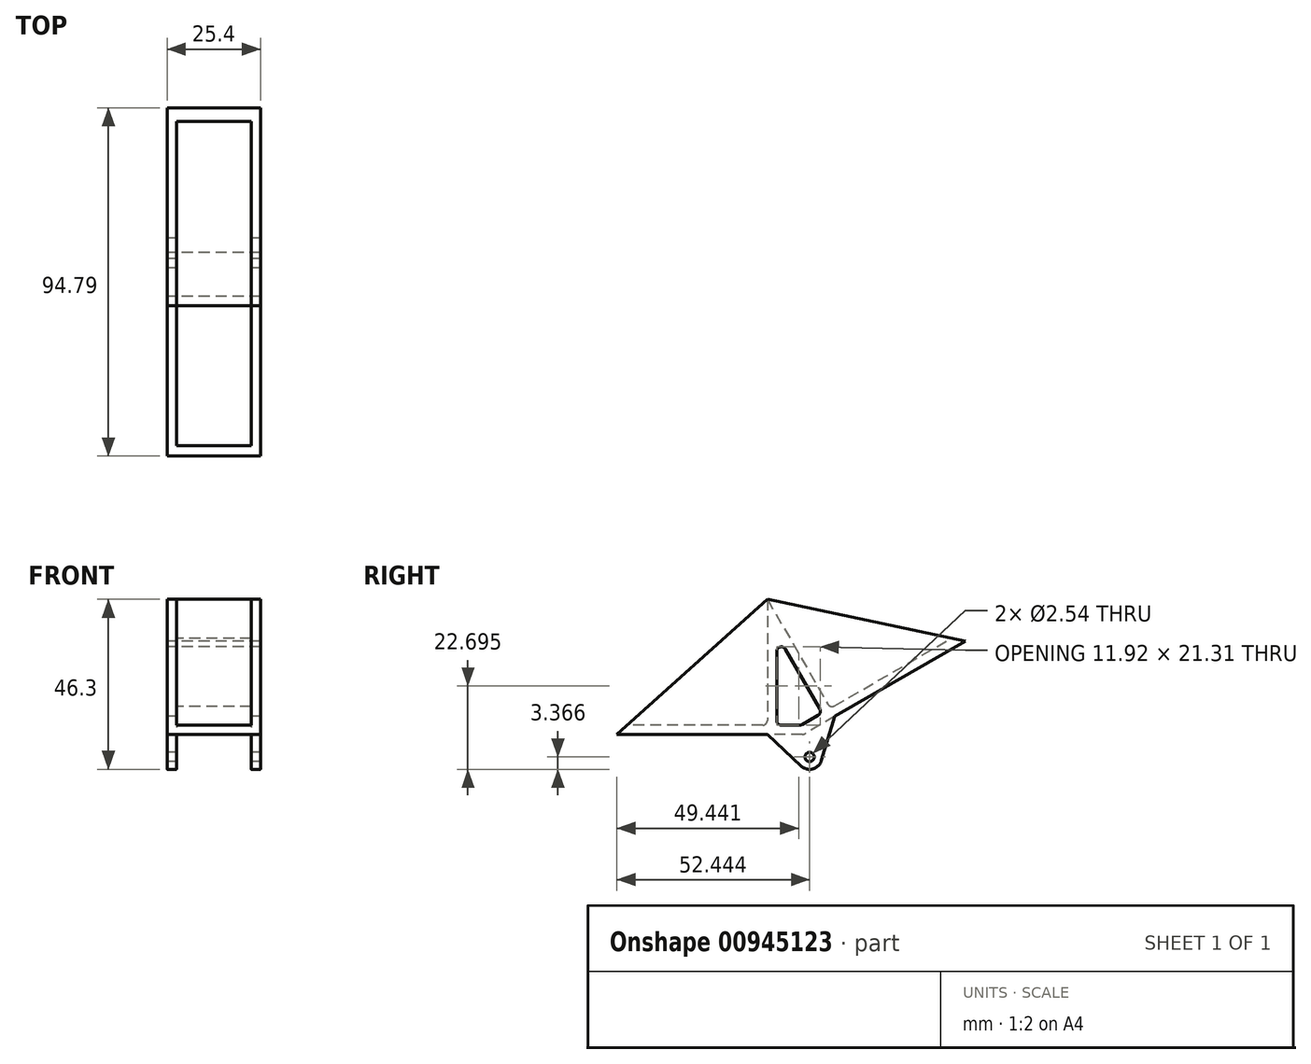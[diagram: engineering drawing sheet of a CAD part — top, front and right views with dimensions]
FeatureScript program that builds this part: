
annotation { "Feature Type Name" : "Feature", "Feature Type Description" : "" }
export const myFeature = defineFeature(function(context is Context, id is Id, definition is map)
    precondition{}
    {
        {
            var Q0;
            Q0=qCreatedBy(makeId("Right.planeOp"),FACE);
            var sketch = newSketch(context, id + "F0", { "sketchPlane" : qUnion([Q0])});
            skLineSegment(sketch, "E0", {"start": v(-9.86, 0) * mm, "end": v(-50.8, 0) * mm});
            skLineSegment(sketch, "E1", {"start": v(8.54, 4.93) * mm, "end": v(44, 25.4) * mm});
            skLineSegment(sketch, "E2", {"start": v(0, 0) * mm, "end": v(-9.86, 36.8) * mm, "construction": true});
            skLineSegment(sketch, "E3", {"start": v(-50.8, 0) * mm, "end": v(-9.86, 36.8) * mm});
            skLineSegment(sketch, "E4", {"start": v(-9.86, 36.8) * mm, "end": v(-8.36, 36.48) * mm});
            skLineSegment(sketch, "E5", {"start": v(-6.05, 2.54) * mm, "end": v(-1.02, 2.54) * mm});
            skLineSegment(sketch, "E6", {"start": v(-0.39, 2.71) * mm, "end": v(3.97, 5.23) * mm});
            skLineSegment(sketch, "E7.trimOffspring", {"start": v(-8.36, 36.48) * mm, "end": v(44, 25.4) * mm});
            skLineSegment(sketch, "E8", {"start": v(-9.86, 36.8) * mm, "end": v(-9.86, 3.81) * mm});
            skLineSegment(sketch, "E9", {"start": v(-9.86, 36.8) * mm, "end": v(6.63, 8.23) * mm});
            skLineSegment(sketch, "E10", {"start": v(-7.32, 3.81) * mm, "end": v(-7.32, 22.58) * mm});
            skLineSegment(sketch, "E11", {"start": v(4.44, 6.96) * mm, "end": v(-4.95, 23.22) * mm});
            skLineSegment(sketch, "E12", {"start": v(0, 0) * mm, "end": v(2.51, -9.38) * mm, "construction": true});
            skLineSegment(sketch, "E13", {"start": v(-0.65, -8.6) * mm, "end": v(-9.86, 0) * mm});
            skLineSegment(sketch, "E14", {"start": v(4.86, -7.12) * mm, "end": v(8.54, 4.93) * mm});
            skLineSegment(sketch, "E15", {"start": v(1.64, -6.13) * mm, "end": v(9.67, -3.98) * mm, "construction": true});
            skArc(sketch, "E16", {"start": v(-0.65, -8.6) * mm, "mid": v(2.51, -9.38) * mm, "end": v(4.86, -7.12) * mm});
            skCircle(sketch, "E17", {"center": v(1.64, -6.13) * mm, "radius": 1.27 * mm});
            skPoint(sketch, "E18.orphan", {"position": v(3.29, -12.27) * mm});
            skArc(sketch, "E19.filletArc", {"start": v(-7.32, 3.81) * mm, "mid": v(-6.95, 2.91) * mm, "end": v(-6.05, 2.54) * mm});
            skArc(sketch, "E20.filletArc", {"start": v(3.97, 5.23) * mm, "mid": v(4.56, 6) * mm, "end": v(4.44, 6.96) * mm});
            skPoint(sketch, "E21.visualSharp", {"position": v(-7.32, 27.32) * mm});
            skArc(sketch, "E21.filletArc", {"start": v(-4.95, 23.22) * mm, "mid": v(-6.38, 23.8) * mm, "end": v(-7.32, 22.58) * mm});
            skLineSegment(sketch, "E22", {"start": v(8.37, 7.77) * mm, "end": v(40.28, 26.19) * mm});
            skArc(sketch, "E23.filletArc", {"start": v(6.63, 8.23) * mm, "mid": v(7.4, 7.64) * mm, "end": v(8.37, 7.77) * mm});
            skLineSegment(sketch, "E24", {"start": v(-11.13, 2.54) * mm, "end": v(-47.97, 2.54) * mm});
            skArc(sketch, "E25.filletArc", {"start": v(-11.13, 2.54) * mm, "mid": v(-10.23, 2.91) * mm, "end": v(-9.86, 3.81) * mm});
            skPoint(sketch, "E26.visualSharp", {"position": v(-0.68, 2.54) * mm});
            skArc(sketch, "E26.filletArc", {"start": v(-1.02, 2.54) * mm, "mid": v(-0.7, 2.58) * mm, "end": v(-0.39, 2.71) * mm});
            skSolve(sketch);
        }
        {
            var Q0;
            {var subQ0=sQuery(id+"F0.wireOp",EDGE,"E3");var subQ1=sQuery(id+"F0.wireOp",EDGE,"E0");var subQ2=makeQuery(id+"F0.imprint","INTERSECT",VERTEX,{"derivedFrom":[subQ1,subQ0]});Q0=makeQuery(id+"F0.imprint","IMPRINT",FACE,{"disambiguationData":[TD([[makeQuery(id+"F0.imprint","IMPRINT",EDGE,{"disambiguationData":[TD([[subQ2,1.0]])],"derivedFrom":subQ1}),-1.0]])]});}
            var Q1;
            {var subQ0=sQuery(id+"F0.wireOp",EDGE,"E4");var subQ1=sQuery(id+"F0.wireOp",EDGE,"E1");var subQ2=makeQuery(id+"F0.imprint","INTERSECT",VERTEX,{"derivedFrom":[subQ1,subQ0]});Q1=makeQuery(id+"F0.imprint","IMPRINT",FACE,{"disambiguationData":[TD([[makeQuery(id+"F0.imprint","IMPRINT",EDGE,{"disambiguationData":[TD([[subQ2,1.0]])],"derivedFrom":subQ1}),1.0]])]});}
            var Q2;
            {var subQ0=sQuery(id+"F0.wireOp",EDGE,"E3");var subQ5=sQuery(id+"F0.wireOp",EDGE,"mqJMZl8p-9VAi-v6qv-n27a-5pC9XECVYwVC");var subQ6=makeQuery(id+"F0.imprint","INTERSECT",VERTEX,{"derivedFrom":[subQ0,subQ5]});Q2=makeQuery(id+"F0.imprint","IMPRINT",FACE,{"disambiguationData":[TD([[makeQuery(id+"F0.imprint","IMPRINT",EDGE,{"disambiguationData":[TD([[subQ6,-1.0]])],"derivedFrom":subQ5}),1.0]])]});}
            var Q3;
            {var subQ0=sQuery(id+"F0.wireOp",EDGE,"E4");var subQ5=sQuery(id+"F0.wireOp",EDGE,"HMWGG6RR-jJKV-HD6m-htNB-dgS0oFNWxqNd");var subQ6=makeQuery(id+"F0.imprint","INTERSECT",VERTEX,{"derivedFrom":[subQ0,subQ5]});Q3=makeQuery(id+"F0.imprint","IMPRINT",FACE,{"disambiguationData":[TD([[makeQuery(id+"F0.imprint","IMPRINT",EDGE,{"disambiguationData":[TD([[subQ6,1.0]])],"derivedFrom":subQ5}),1.0]])]});}
            var Q4;
            {var subQ0=sQuery(id+"F0.wireOp",EDGE,"2FNbGdT5-oPHb-nvho-1RKC-4htPkp7pQmcZ");var subQ1=sQuery(id+"F0.wireOp",EDGE,"E2");var subQ2=makeQuery(id+"F0.imprint","INTERSECT",VERTEX,{"derivedFrom":[subQ1,subQ0]});Q4=makeQuery(id+"F0.imprint","IMPRINT",FACE,{"disambiguationData":[TD([[makeQuery(id+"F0.imprint","IMPRINT",EDGE,{"disambiguationData":[TD([[subQ2,-1.0]])],"derivedFrom":subQ1}),1.0]])]});}
            var Q5;
            {var subQ0=sQuery(id+"F0.wireOp",EDGE,"3LhKCgj5-OBTh-ZDzE-TMFg-cuMuyVttlFuA");var subQ1=sQuery(id+"F0.wireOp",EDGE,"HMWGG6RR-jJKV-HD6m-htNB-dgS0oFNWxqNd");var subQ2=makeQuery(id+"F0.imprint","INTERSECT",VERTEX,{"derivedFrom":[subQ1,subQ0]});Q5=makeQuery(id+"F0.imprint","IMPRINT",FACE,{"disambiguationData":[TD([[makeQuery(id+"F0.imprint","IMPRINT",EDGE,{"disambiguationData":[TD([[subQ2,-1.0]])],"derivedFrom":subQ1}),1.0]])]});}
            extrude(context, id + "F1", {"entities" : qUnion([Q0, Q1, Q2, Q3, Q4, Q5]), "depth" : 25.4 * mm, "offsetDistance" : 25.4 * mm});
        }
        {
            var Q0;
            {var subQ0=sQuery(id+"F0.wireOp",EDGE,"E8");Q0=makeQuery(id+"F0.imprint","IMPRINT",FACE,{"disambiguationData":[TD([[makeQuery(id+"F0.imprint","IMPRINT",EDGE,{"derivedFrom":subQ0}),-1.0]])]});}
            var Q1;
            {var subQ2=sQuery(id+"F0.wireOp",EDGE,"E4");Q1=makeQuery(id+"F0.imprint","IMPRINT",FACE,{"disambiguationData":[TD([[makeQuery(id+"F0.imprint","IMPRINT",EDGE,{"derivedFrom":subQ2}),-1.0]])]});}
            extrude(context, id + "F2", {"entities" : qUnion([Q0, Q1]), "operationType" : NewBodyOperationType.ADD, "depth" : 2.54 * mm, "offsetDistance" : 25.4 * mm});
        }
        {
            var Q0;
            Q0=makeQuery(id+"F1.opExtrude","CAP_FACE",FACE,{"disambiguationData":[OSD([sQuery(id+"F0.wireOp",EDGE,"E0"),sQuery(id+"F0.wireOp",EDGE,"E1"),sQuery(id+"F0.wireOp",EDGE,"E3"),sQuery(id+"F0.wireOp",EDGE,"E5"),sQuery(id+"F0.wireOp",EDGE,"E6"),sQuery(id+"F0.wireOp",EDGE,"E7.trimOffspring"),sQuery(id+"F0.wireOp",EDGE,"E8"),sQuery(id+"F0.wireOp",EDGE,"E9"),sQuery(id+"F0.wireOp",EDGE,"E10"),sQuery(id+"F0.wireOp",EDGE,"E11"),sQuery(id+"F0.wireOp",EDGE,"E13"),sQuery(id+"F0.wireOp",EDGE,"E14"),sQuery(id+"F0.wireOp",EDGE,"E16"),sQuery(id+"F0.wireOp",EDGE,"E17"),sQuery(id+"F0.wireOp",EDGE,"E19.filletArc"),sQuery(id+"F0.wireOp",EDGE,"E20.filletArc"),sQuery(id+"F0.wireOp",EDGE,"E21.filletArc"),sQuery(id+"F0.wireOp",EDGE,"E22"),sQuery(id+"F0.wireOp",EDGE,"E23.filletArc"),sQuery(id+"F0.wireOp",EDGE,"E24"),sQuery(id+"F0.wireOp",EDGE,"E25.filletArc"),sQuery(id+"F0.wireOp",EDGE,"E26.filletArc")])],"isStart":false});
            var sketch = newSketch(context, id + "F3", { "sketchPlane" : qUnion([Q0])});
            skLineSegment(sketch, "E27.0.0", {"start": v(-9.86, 36.8) * mm, "end": v(-47.97, 2.54) * mm});
            skLineSegment(sketch, "E27.0.1", {"start": v(-47.97, 2.54) * mm, "end": v(-11.13, 2.54) * mm});
            skArc(sketch, "E27.0.2", {"start": v(-11.13, 2.54) * mm, "mid": v(-10.23, 2.91) * mm, "end": v(-9.86, 3.81) * mm});
            skLineSegment(sketch, "E27.0.3", {"start": v(-9.86, 3.81) * mm, "end": v(-9.86, 36.8) * mm});
            skLineSegment(sketch, "E28.0.0", {"start": v(40.28, 26.19) * mm, "end": v(-9.86, 36.8) * mm});
            skLineSegment(sketch, "E28.0.1", {"start": v(-9.86, 36.8) * mm, "end": v(6.63, 8.23) * mm});
            skArc(sketch, "E28.0.2", {"start": v(6.63, 8.23) * mm, "mid": v(7.4, 7.64) * mm, "end": v(8.37, 7.77) * mm});
            skLineSegment(sketch, "E28.0.3", {"start": v(8.37, 7.77) * mm, "end": v(40.28, 26.19) * mm});
            skSolve(sketch);
        }
        {
            var Q0;
            Q0=makeQuery(id+"F3.imprint","IMPRINT",FACE,{"disambiguationData":[TD([[makeQuery(id+"F3.imprint","IMPRINT",EDGE,{"derivedFrom":sQuery(id+"F3.wireOp",EDGE,"E27.0.0")}),1.0]])]});
            var Q1;
            Q1=makeQuery(id+"F3.imprint","IMPRINT",FACE,{"disambiguationData":[TD([[makeQuery(id+"F3.imprint","IMPRINT",EDGE,{"derivedFrom":sQuery(id+"F3.wireOp",EDGE,"E28.0.0")}),1.0]])]});
            extrude(context, id + "F4", {"entities" : qUnion([Q0, Q1]), "operationType" : NewBodyOperationType.ADD, "oppositeDirection" : true, "depth" : 2.54 * mm, "offsetDistance" : 25.4 * mm});
        }
        {
            var Q0;
            Q0=qCreatedBy(makeId("Right.planeOp"),FACE);
            var sketch = newSketch(context, id + "F5", { "sketchPlane" : qUnion([Q0])});
            skLineSegment(sketch, "E29.0.2", {"start": v(8.54, 4.93) * mm, "end": v(0.3, 0.17) * mm});
            skLineSegment(sketch, "E29.0.3", {"start": v(8.54, 4.93) * mm, "end": v(4.86, -7.12) * mm});
            skArc(sketch, "E29.0.4", {"start": v(4.86, -7.12) * mm, "mid": v(2.51, -9.38) * mm, "end": v(-0.65, -8.6) * mm});
            skLineSegment(sketch, "E29.0.5", {"start": v(-0.65, -8.6) * mm, "end": v(-9.86, 0) * mm});
            skLineSegment(sketch, "E29.0.6", {"start": v(-0.34, 0) * mm, "end": v(-9.86, 0) * mm});
            skArc(sketch, "E30.filletArc", {"start": v(-0.34, 0) * mm, "mid": v(-0.01, 0.04) * mm, "end": v(0.3, 0.17) * mm});
            skPoint(sketch, "E29.0.1.end.orphan", {"position": v(44, 25.4) * mm});
            skPoint(sketch, "E29.0.0.end.orphan", {"position": v(-9.86, 36.8) * mm});
            skPoint(sketch, "E29.0.0.start.orphan", {"position": v(-50.8, 0) * mm});
            skSolve(sketch);
        }
        {
            var Q0;
            Q0=makeQuery(id+"F5.imprint","IMPRINT",FACE,{"disambiguationData":[TD([[makeQuery(id+"F5.imprint","IMPRINT",EDGE,{"derivedFrom":sQuery(id+"F5.wireOp",EDGE,"E29.0.2")}),1.0]])]});
            cPlane(context, id + "F6", {"entities" : qUnion([Q0]), "cplaneType" : CPlaneType.OFFSET, "offset" : 2.54 * mm, "width" : 152.4 * mm, "height" : 152.4 * mm});
        }
        {
            var Q0;
            Q0=qCreatedBy(id+"F6.planeOp",FACE);
            var sketch = newSketch(context, id + "F7", { "sketchPlane" : qUnion([Q0])});
            skArc(sketch, "E31.0.0", {"start": v(0.3, 0.17) * mm, "mid": v(-0.01, 0.04) * mm, "end": v(-0.34, 0) * mm});
            skLineSegment(sketch, "E31.0.1", {"start": v(-0.34, 0) * mm, "end": v(-9.86, 0) * mm});
            skLineSegment(sketch, "E31.0.2", {"start": v(-9.86, 0) * mm, "end": v(-0.65, -8.6) * mm});
            skArc(sketch, "E31.0.3", {"start": v(-0.65, -8.6) * mm, "mid": v(2.51, -9.38) * mm, "end": v(4.86, -7.12) * mm});
            skLineSegment(sketch, "E31.0.4", {"start": v(4.86, -7.12) * mm, "end": v(8.54, 4.93) * mm});
            skLineSegment(sketch, "E31.0.5", {"start": v(8.54, 4.93) * mm, "end": v(0.3, 0.17) * mm});
            skSolve(sketch);
        }
        {
            var Q0;
            Q0 = qSketchRegion(id + "F7", true);
            extrude(context, id + "F8", {"entities" : qUnion([Q0]), "operationType" : NewBodyOperationType.REMOVE, "depth" : 20.32 * mm, "offsetDistance" : 25.4 * mm});
        }
    });
